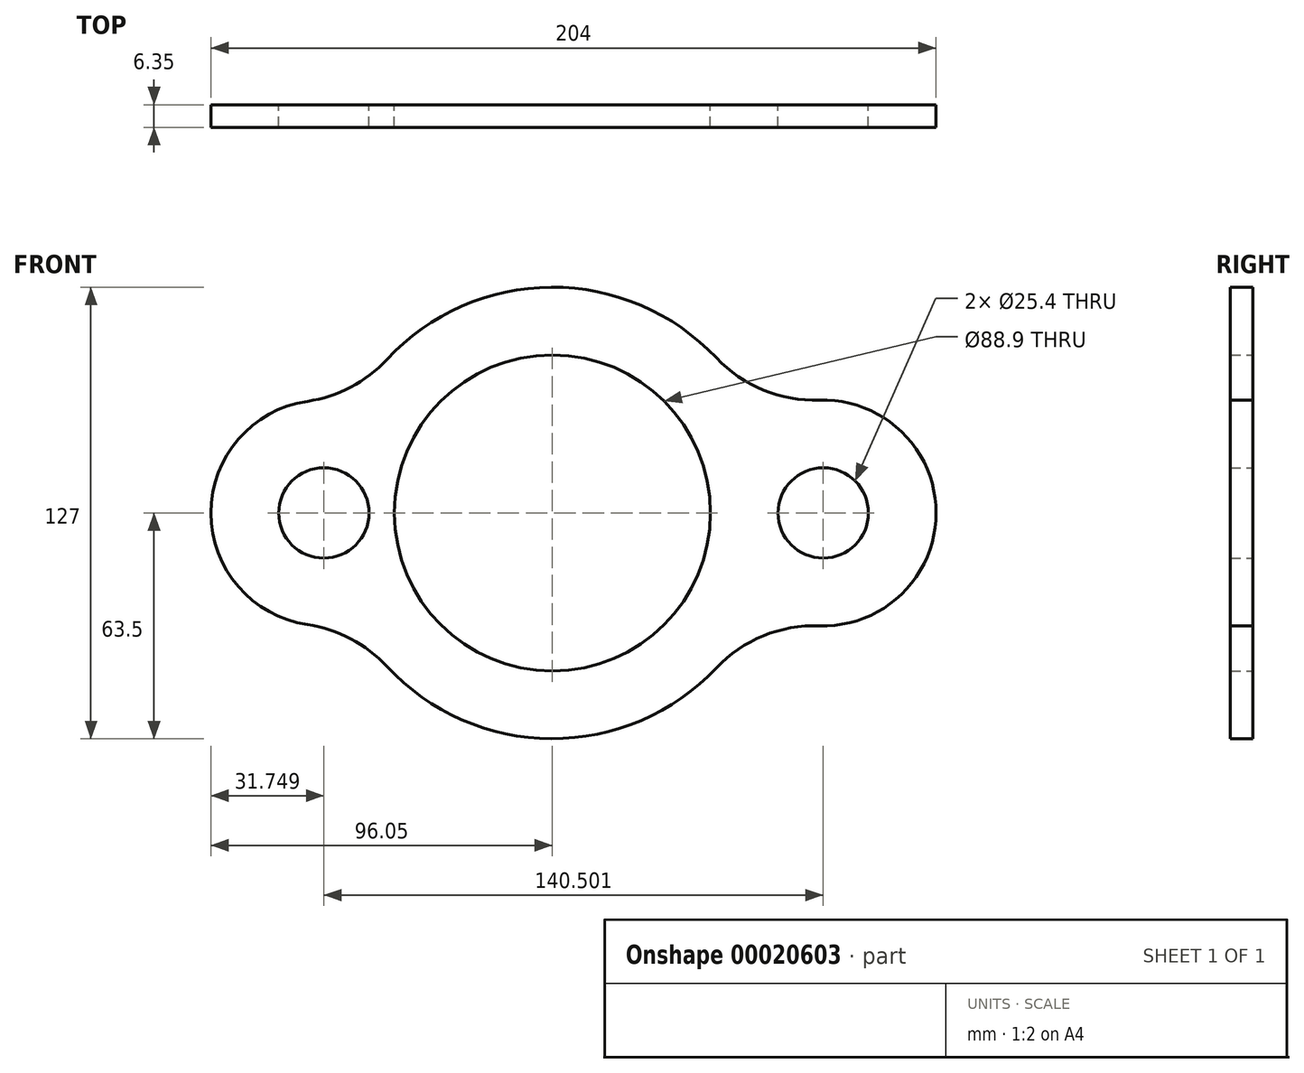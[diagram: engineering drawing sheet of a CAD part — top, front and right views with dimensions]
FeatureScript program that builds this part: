
annotation { "Feature Type Name" : "Feature", "Feature Type Description" : "" }
export const myFeature = defineFeature(function(context is Context, id is Id, definition is map)
    precondition{}
    {
        {
            var Q0;
            Q0=qCreatedBy(makeId("Front.planeOp"),FACE);
            var sketch = newSketch(context, id + "F0", { "sketchPlane" : qUnion([Q0])});
            skCircle(sketch, "E0", {"center": v(0, 0) * mm, "radius": 44.45 * mm});
            skArc(sketch, "E1", {"start": v(46.14, 43.63) * mm, "mid": v(-0.3, 63.5) * mm, "end": v(-46.55, 43.2) * mm});
            skCircle(sketch, "E2", {"center": v(-64.3, 0) * mm, "radius": 12.7 * mm});
            skCircle(sketch, "E3", {"center": v(76.2, 0) * mm, "radius": 12.7 * mm});
            skArc(sketch, "E4", {"start": v(-68.93, 31.41) * mm, "mid": v(-96.05, 0) * mm, "end": v(-68.93, -31.41) * mm});
            skArc(sketch, "E5", {"start": v(75.12, -31.73) * mm, "mid": v(107.95, 0) * mm, "end": v(75.12, 31.73) * mm});
            skArc(sketch, "E6.trimOffspring", {"start": v(-46.55, -43.2) * mm, "mid": v(-0.3, -63.5) * mm, "end": v(46.14, -43.63) * mm});
            skPoint(sketch, "E7.start.orphan", {"position": v(-150.33, 0) * mm});
            skPoint(sketch, "E8.visualSharp", {"position": v(-55.67, 30.55) * mm});
            skArc(sketch, "E8.filletArc", {"start": v(-68.93, 31.41) * mm, "mid": v(-56.73, 35.39) * mm, "end": v(-46.55, 43.2) * mm});
            skPoint(sketch, "E9.visualSharp", {"position": v(-55.67, -30.55) * mm});
            skArc(sketch, "E9.filletArc", {"start": v(-46.55, -43.2) * mm, "mid": v(-56.73, -35.39) * mm, "end": v(-68.93, -31.41) * mm});
            skPoint(sketch, "E10.visualSharp", {"position": v(57.94, -25.98) * mm});
            skArc(sketch, "E10.filletArc", {"start": v(75.12, -31.73) * mm, "mid": v(59.35, -34.56) * mm, "end": v(46.14, -43.63) * mm});
            skPoint(sketch, "E11.visualSharp", {"position": v(57.94, 25.98) * mm});
            skArc(sketch, "E11.filletArc", {"start": v(46.14, 43.63) * mm, "mid": v(59.35, 34.56) * mm, "end": v(75.12, 31.73) * mm});
            skSolve(sketch);
        }
        {
            var Q0;
            Q0=makeQuery(id+"F0.imprint","IMPRINT",FACE,{"disambiguationData":[TD([[makeQuery(id+"F0.imprint","IMPRINT",EDGE,{"derivedFrom":sQuery(id+"F0.wireOp",EDGE,"E0")}),-1.0]])]});
            extrude(context, id + "F1", {"entities" : qUnion([Q0]), "depth" : 6.35 * mm});
        }
    });
